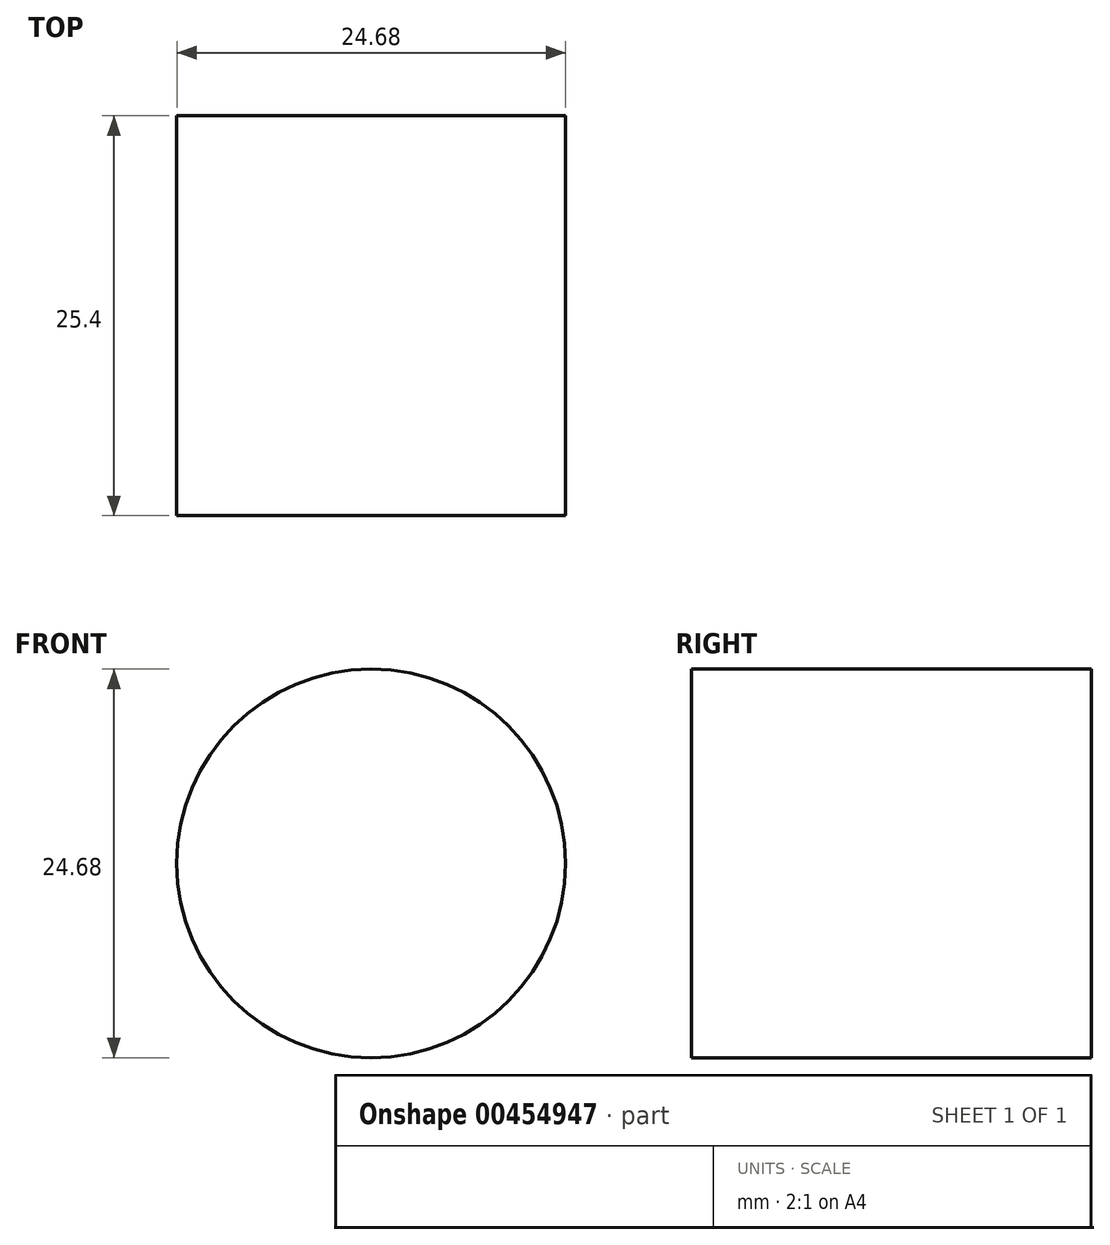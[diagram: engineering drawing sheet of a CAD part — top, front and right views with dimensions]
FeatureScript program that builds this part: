
annotation { "Feature Type Name" : "Feature", "Feature Type Description" : "" }
export const myFeature = defineFeature(function(context is Context, id is Id, definition is map)
    precondition{}
    {
        {
            var Q0;
            Q0=qCreatedBy(makeId("Front.planeOp"),FACE);
            var sketch = newSketch(context, id + "F0", { "sketchPlane" : qUnion([Q0])});
            skCircle(sketch, "E0", {"center": v(0, 0) * mm, "radius": 12.34 * mm});
            skSolve(sketch);
        }
        {
            var Q0;
            Q0 = qSketchRegion(id + "F0", true);
            extrude(context, id + "F1", {"entities" : qUnion([Q0]), "depth" : 25.4 * mm});
        }
    });
